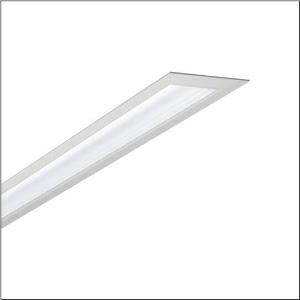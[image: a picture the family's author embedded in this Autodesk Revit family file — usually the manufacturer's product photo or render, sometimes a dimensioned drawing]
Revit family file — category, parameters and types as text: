
# Revit family: silica_r_5mx11bd2w4a_6c5b
name_source: partatom
category: Lighting Fixtures
units: mm (PartAtom-declared; Revit-internal decimal feet)

## family parameters
Cut with Voids When Loaded = No
Host = Face
Light Source = No
Part Type = Normal
Room Calculation Point = No
Round Connector Dimension = Use Diameter
Shared = No

## types (1)
- --- (1 x LED, 9910 lm, 60.1 W, 4000K)
    Apparent Load = 60 VA
    CIE Flux Codes = 82 97 100 100 100
    Color Rendering = 80
    Color Temperature = 4000K
    Default Elevation = 1800 mm
    Description = Silica®, office luminaire, of aluminium, light emission: direct distribution, primary light characteristic: symmetric, installation type: recessed, LED, rated luminous flux: 9.910lm, luminous efficacy: 165lm/W, light colour: 840, colour temperature: 4000K, control gear: DALI 2, with terminal, 3+2-pole, max. 2.5mm², mains connection: 230V, AC, 50/60Hz, rated input power: 60W, luminaire housing, of aluminium, matt pure white (RAL 9010), length: 2.864mm, width: 93mm, height: 60mm, end cap, of diecast zinc, pure white (RAL 9010), protection rating (complete): IP20, insulation class (complete): insulation class I (protective earthing), certification: CE, permissible operating ambient temperature: 0..+35°C, standard: EN 50419, packaging unit: 1 piece
    Height = 0 mm  [stored 0 ft]
    Lamp = 1 x LED
    Lamp Light Flux = 9910 lm
    Lamp Power = 60.1 W
    Lamp count = 1
    Length = 2865 mm
    Luminous efficacy = 165 lm/W
    Manufacturer = Siteco
    ModVariant = No
    Model = 5MX11BD2W4A
    Mounting Place = Ceiling
    Mounting Type = Recessed
    Number of Poles = 1
    OnlyDefault = Yes
    Power Factor = 1
    Product Name = Silica®
    Product group = office luminaire | ceiling recessed
    ProductGroupID = 401
    Protection Class = Protection class I
    Protection Degree = IP 20
    RLX_Detail_Level = 1
    RLX_Emergency_Light_Flux = 0 lm
    RLX_Emergency_Type = 0
    RLX_Emergency_Type_DB = No
    RlxData = <blob elided: 24325 chars, md5=4fde39fc>
    Socket = socket
    Standby Power = 0 W
    System Light Flux = 9910 lm
    System Power = 60 W
    Type Comments = factory setting: luminous flux: 100 % | dim-lin: 254 | 336 mA
    Type Image = l_1004825.jpg
    URL = http://relux.com
    VarID = @adj_198805
    Voltage = 0 V
    Weight = 0.00 kg
    Width = 93 mm

note: [stored X ft] marks values corroborated as IEEE doubles in the binary element streams (Revit-internal decimal feet)

## geometry (parser evidence)
native form markers: Blend x4, Sweep x9
no freeform markers — native parametric forms only
